# Revit family: QF_COMCATER ALL BRANDS_RCB9
name_source: partatom
category: Specialty Equipment
revit_build: Autodesk Revit 2014 (Build: 20140709_2115(x64)
units: mm (PartAtom-declared; Revit-internal decimal feet)

## types (2) — shared parameters
Accessory = No
Assembly Code = E1090320
Depth Actual = 803 mm  [stored 2.63451 ft]
Description = GAS BARBECUE TOP
Gas Flow = 0.0 L/s
Gas Size = 19 mm
Gas Size Flexible = 0 mm
Height Actual = 455 mm
Length Actual = 900 mm  [stored 2.95276 ft]
Manufacturer = TRUEHEAT
Model = RCB9
Type Comments = The Australian owned and designed* Trueheat RC Series of Gas Cooking Equipment has been developed for the restaurant and cafe market with a high quality finish, designed to fulfill the busy demands within a commercial kitchen.
Our team of professionals have designed and engineered the ultimate barbecue by incorporating premium infrared technology. Heavy duty cast iron radiant hoods over powerful gas burners radiate heat to the grates are reversible for angled or flat operation.
100% Flame failure controls included as standard. Piezo ignition included as standard.

## per-type parameters (varying)
| type | BTUH | Gas power kW | Nominal Gas power |
| RCB9_Natural Gas | 23600 W | 23.6 | 23600 W |
| RCB9_LPG | 21500 W | 21.5 | 21500 W |

note: [stored X ft] marks values corroborated as IEEE doubles in the binary element streams (Revit-internal decimal feet)

## geometry (parser evidence)
native form markers: Sweep x5
no freeform markers — native parametric forms only
